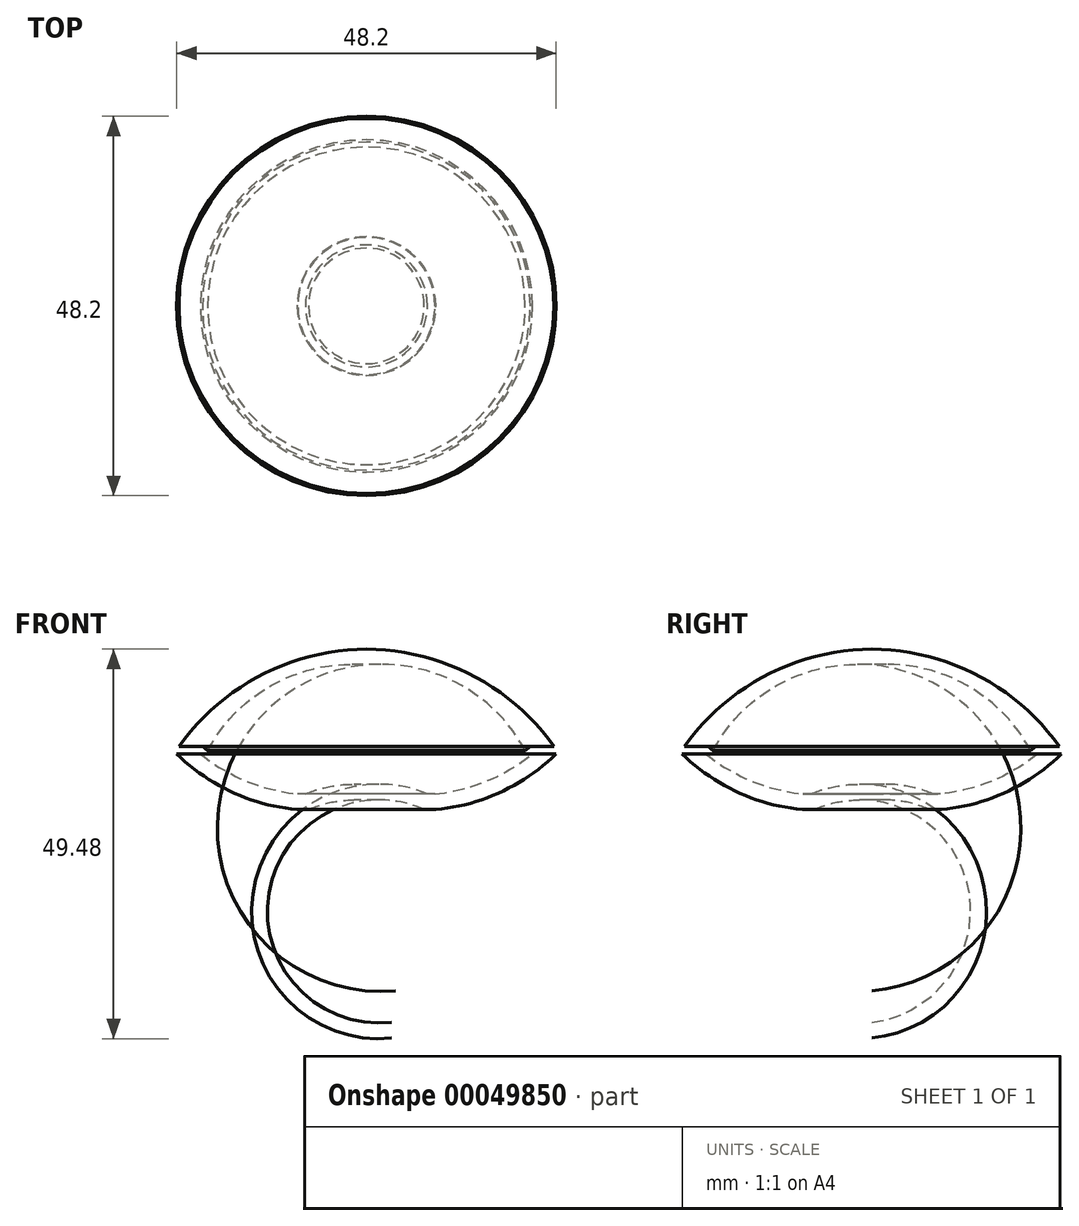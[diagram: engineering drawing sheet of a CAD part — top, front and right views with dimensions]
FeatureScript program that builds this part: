
annotation { "Feature Type Name" : "Feature", "Feature Type Description" : "" }
export const myFeature = defineFeature(function(context is Context, id is Id, definition is map)
    precondition{}
    {
        {
            var Q0;
            Q0=qCreatedBy(makeId("Front.planeOp"),FACE);
            var sketch = newSketch(context, id + "F0", { "sketchPlane" : qUnion([Q0])});
            skArc(sketch, "E0", {"start": v(8.81, -7.09) * mm, "mid": v(17.07, -4.86) * mm, "end": v(24.1, 0) * mm});
            skLineSegment(sketch, "E1", {"start": v(8.81, -7.09) * mm, "end": v(7.34, -7.09) * mm});
            skArc(sketch, "E2", {"start": v(7.34, -7.09) * mm, "mid": v(3.75, -6.03) * mm, "end": v(0, -5.95) * mm});
            skArc(sketch, "E3.0", {"start": v(8.72, -5.09) * mm, "mid": v(15.29, -3.46) * mm, "end": v(21.1, 0) * mm});
            skLineSegment(sketch, "E3.1", {"start": v(8.72, -5.09) * mm, "end": v(7.75, -5.09) * mm});
            skArc(sketch, "E3.2", {"start": v(7.75, -5.09) * mm, "mid": v(3.95, -4.04) * mm, "end": v(0, -3.94) * mm});
            skPoint(sketch, "E4", {"position": v(0, -3.94) * mm});
            skPoint(sketch, "E5", {"position": v(21.1, 0) * mm});
            skLineSegment(sketch, "E6", {"start": v(21.1, 0) * mm, "end": v(24.1, 0) * mm});
            skLineSegment(sketch, "E7", {"start": v(0, -3.94) * mm, "end": v(0, -5.95) * mm});
            skArc(sketch, "E8.0", {"start": v(20.17, 0.41) * mm, "mid": v(20.5, 0.67) * mm, "end": v(20.82, 0.94) * mm});
            skArc(sketch, "E9", {"start": v(20.17, 0.41) * mm, "mid": v(11.72, 8.88) * mm, "end": v(0, 11.3) * mm});
            skLineSegment(sketch, "E10", {"start": v(20.82, 0.94) * mm, "end": v(23.82, 0.94) * mm});
            skLineSegment(sketch, "E11", {"start": v(0, 11.3) * mm, "end": v(0, 13.3) * mm});
            skArc(sketch, "E12", {"start": v(23.82, 0.94) * mm, "mid": v(13.4, 9.98) * mm, "end": v(0, 13.3) * mm});
            skLineSegment(sketch, "E13", {"start": v(0, 0) * mm, "end": v(0, 10.27) * mm, "construction": true});
            skLineSegment(sketch, "E14", {"start": v(0, 14.56) * mm, "end": v(2.5, 14.56) * mm});
            skLineSegment(sketch, "E15", {"start": v(2.5, 14.56) * mm, "end": v(1, 13.77) * mm});
            skLineSegment(sketch, "E16", {"start": v(1, 13.77) * mm, "end": v(1, 13.27) * mm});
            skLineSegment(sketch, "E17", {"start": v(0, 14.56) * mm, "end": v(0, 13.3) * mm});
            skSolve(sketch);
        }
        {
            var Q0;
            Q0=qCreatedBy(makeId("Top.planeOp"),FACE);
            var sketch = newSketch(context, id + "F1", { "sketchPlane" : qUnion([Q0])});
            skCircle(sketch, "E18", {"center": v(0, 0) * mm, "radius": 21.1 * mm});
            skSolve(sketch);
        }
        {
            var Q0;
            Q0=makeQuery(id+"F0.imprint","IMPRINT",FACE,{"disambiguationData":[TD([[makeQuery(id+"F0.imprint","IMPRINT",EDGE,{"derivedFrom":sQuery(id+"F0.wireOp",EDGE,"E0")}),1.0]])]});
            var Q1;
            Q1=makeQuery(id+"F0.imprint","IMPRINT",FACE,{"disambiguationData":[TD([[makeQuery(id+"F0.imprint","IMPRINT",EDGE,{"derivedFrom":sQuery(id+"F0.wireOp",EDGE,"E8.0")}),1.0]])]});
            var Q2;
            Q2=sQuery(id+"F1.wireOp",EDGE,"E18");
            sweep(context, id + "F2", {"profiles" : qUnion([Q0, Q1]), "path" : qUnion([Q2])});
        }
    });
